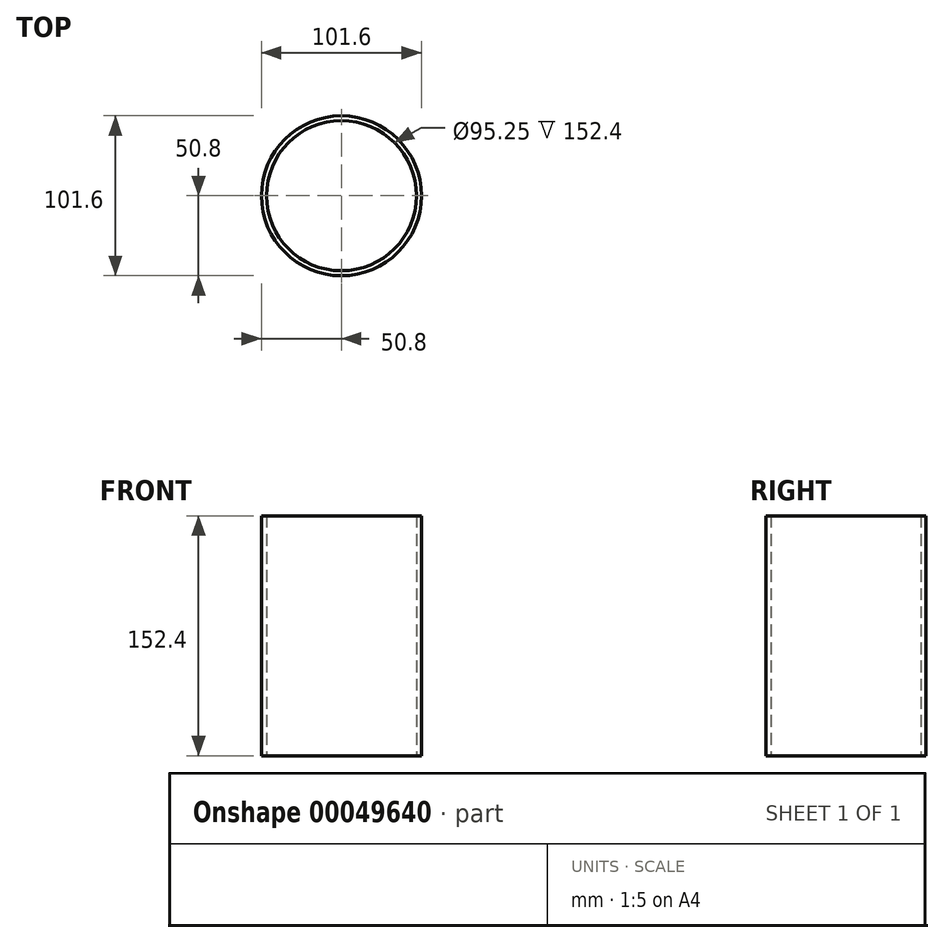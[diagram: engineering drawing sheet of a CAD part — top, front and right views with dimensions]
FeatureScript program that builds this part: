
annotation { "Feature Type Name" : "Feature", "Feature Type Description" : "" }
export const myFeature = defineFeature(function(context is Context, id is Id, definition is map)
    precondition{}
    {
        {
            var Q0;
            Q0=qCreatedBy(makeId("Front.planeOp"),FACE);
            var sketch = newSketch(context, id + "F0", { "sketchPlane" : qUnion([Q0])});
            skLineSegment(sketch, "E0", {"start": v(0, 0) * mm, "end": v(0, 73.02) * mm, "construction": true});
            skLineSegment(sketch, "E1.bottom", {"start": v(47.63, 0) * mm, "end": v(50.8, 0) * mm});
            skLineSegment(sketch, "E1.top", {"start": v(47.62, 152.4) * mm, "end": v(50.8, 152.4) * mm});
            skLineSegment(sketch, "E1.left", {"start": v(47.63, 0) * mm, "end": v(47.62, 152.4) * mm});
            skLineSegment(sketch, "E1.right", {"start": v(50.8, 0) * mm, "end": v(50.8, 152.4) * mm});
            skSolve(sketch);
        }
        {
            var Q0;
            Q0=makeQuery(id+"F0.imprint","IMPRINT",FACE,{"disambiguationData":[TD([[makeQuery(id+"F0.imprint","IMPRINT",EDGE,{"derivedFrom":sQuery(id+"F0.wireOp",EDGE,"E1.bottom")}),1.0]])]});
            var Q1;
            Q1=sQuery(id+"F0.wireOp",EDGE,"E0");
            revolve(context, id + "F1", {"entities" : qUnion([Q0]), "axis" : qUnion([Q1]), "revolveType" : RevolveType.FULL});
        }
    });
